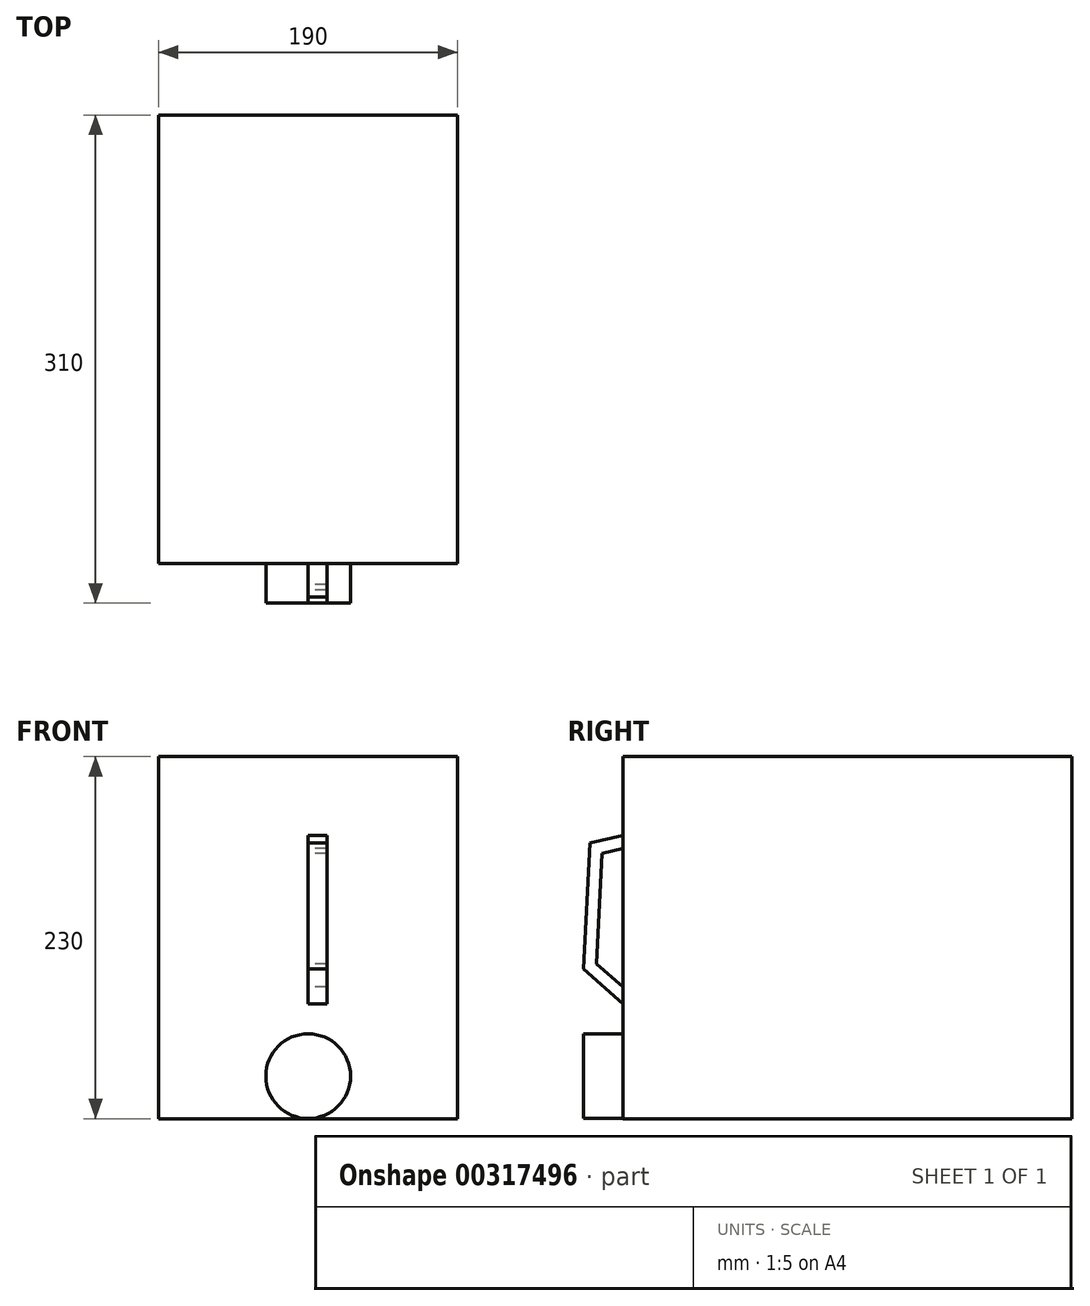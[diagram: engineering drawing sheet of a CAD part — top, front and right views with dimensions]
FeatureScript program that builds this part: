
annotation { "Feature Type Name" : "Feature", "Feature Type Description" : "" }
export const myFeature = defineFeature(function(context is Context, id is Id, definition is map)
    precondition{}
    {
        {
            var Q0;
            Q0=qCreatedBy(makeId("Top.planeOp"),FACE);
            var sketch = newSketch(context, id + "F0", { "sketchPlane" : qUnion([Q0])});
            skLineSegment(sketch, "E0.bottom", {"start": v(95, -142.5) * mm, "end": v(-95, -142.5) * mm});
            skLineSegment(sketch, "E0.top", {"start": v(95, 142.5) * mm, "end": v(-95, 142.5) * mm});
            skLineSegment(sketch, "E0.left", {"start": v(95, -142.5) * mm, "end": v(95, 142.5) * mm});
            skLineSegment(sketch, "E0.right", {"start": v(-95, -142.5) * mm, "end": v(-95, 142.5) * mm});
            skPoint(sketch, "E0.middle", {"position": v(0, 0) * mm});
            skSolve(sketch);
        }
        {
            var Q0;
            Q0 = qSketchRegion(id + "F0", true);
            extrude(context, id + "F1", {"entities" : qUnion([Q0]), "depth" : 230 * mm});
        }
        {
            var Q0;
            Q0=makeQuery(id+"F1.opExtrude","SWEPT_FACE",FACE,{"disambiguationData":[OSD([sQuery(id+"F0.wireOp",EDGE,"E0.bottom")])]});
            var sketch = newSketch(context, id + "F2", { "sketchPlane" : qUnion([Q0])});
            skCircle(sketch, "E1", {"center": v(0, 27) * mm, "radius": 26.9 * mm});
            skSolve(sketch);
        }
        {
            var Q0;
            Q0 = qSketchRegion(id + "F2", true);
            extrude(context, id + "F3", {"entities" : qUnion([Q0]), "operationType" : NewBodyOperationType.ADD, "depth" : 25 * mm});
        }
        {
            var Q0;
            Q0=qCreatedBy(makeId("Right.planeOp"),FACE);
            var sketch = newSketch(context, id + "F4", { "sketchPlane" : qUnion([Q0])});
            skLineSegment(sketch, "E2", {"start": v(-142.5, 180) * mm, "end": v(-163.5, 175) * mm});
            skLineSegment(sketch, "E3", {"start": v(-163.5, 175) * mm, "end": v(-167.5, 95) * mm});
            skLineSegment(sketch, "E4", {"start": v(-167.5, 95) * mm, "end": v(-142.5, 73) * mm});
            skLineSegment(sketch, "E5", {"start": v(-142.5, 73) * mm, "end": v(-142.5, 83.66) * mm});
            skLineSegment(sketch, "E6.0", {"start": v(-159.32, 98.46) * mm, "end": v(-142.5, 83.66) * mm});
            skLineSegment(sketch, "E6.1", {"start": v(-155.8, 168.6) * mm, "end": v(-159.32, 98.46) * mm});
            skLineSegment(sketch, "E6.2", {"start": v(-142.5, 171.78) * mm, "end": v(-155.8, 168.6) * mm});
            skLineSegment(sketch, "E7.trimOffspring", {"start": v(-142.5, 171.78) * mm, "end": v(-142.5, 180) * mm});
            skSolve(sketch);
        }
        {
            var Q0;
            Q0 = qSketchRegion(id + "F4", true);
            extrude(context, id + "F5", {"entities" : qUnion([Q0]), "operationType" : NewBodyOperationType.ADD, "depth" : 12 * mm});
        }
    });
